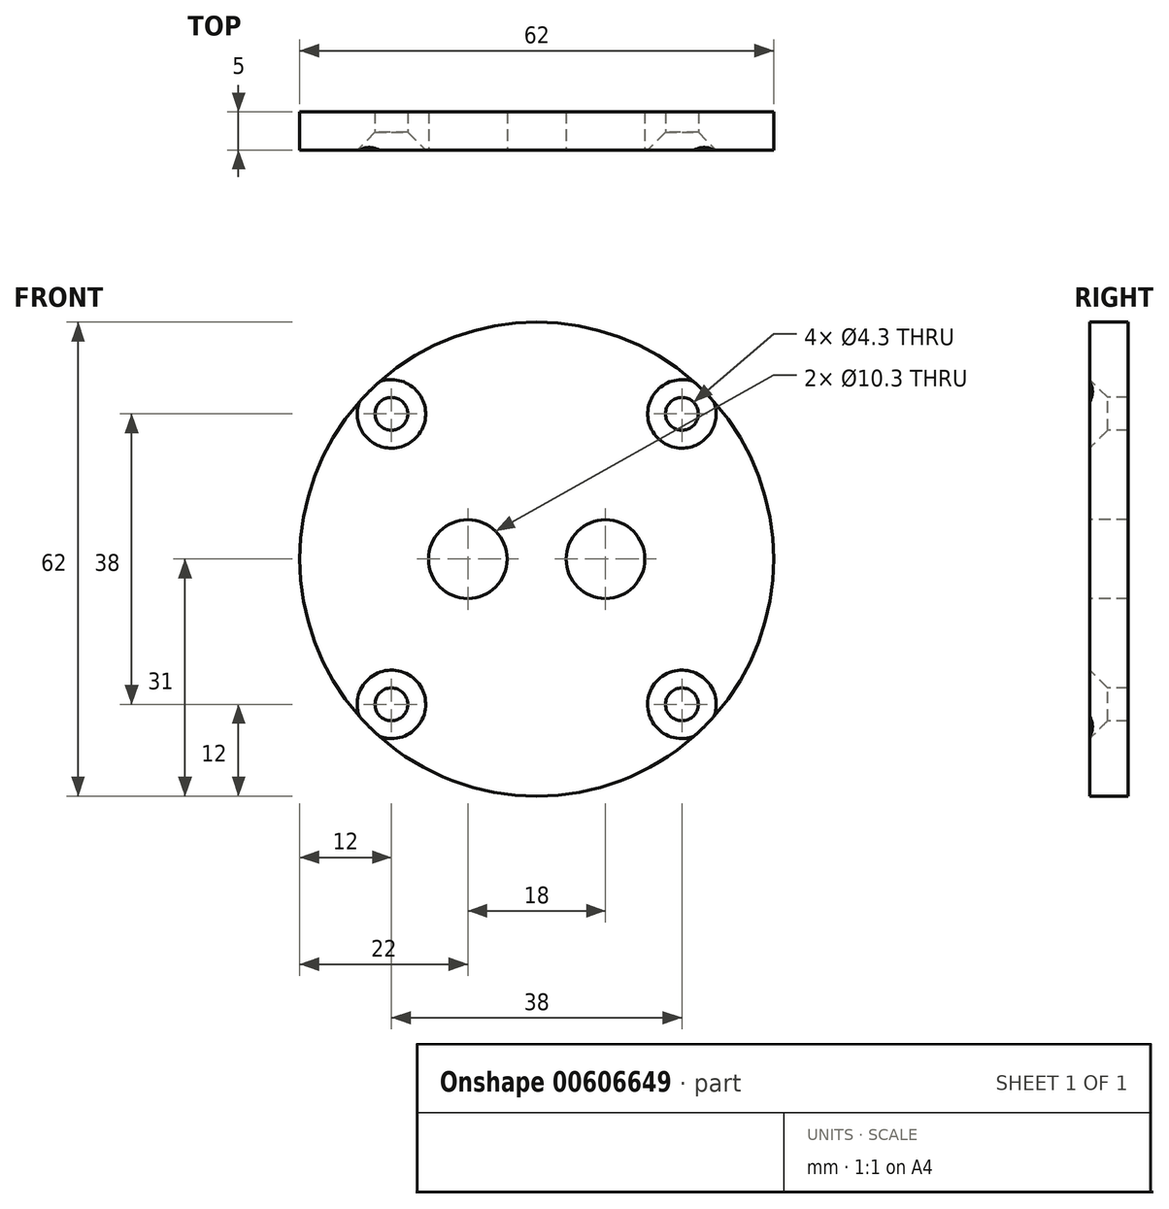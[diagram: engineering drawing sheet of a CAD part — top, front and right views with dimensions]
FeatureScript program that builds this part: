
annotation { "Feature Type Name" : "Feature", "Feature Type Description" : "" }
export const myFeature = defineFeature(function(context is Context, id is Id, definition is map)
    precondition{}
    {
        {
            var Q0;
            Q0=qCreatedBy(makeId("Front.planeOp"),FACE);
            var sketch = newSketch(context, id + "F0", { "sketchPlane" : qUnion([Q0])});
            skCircle(sketch, "E0", {"center": v(0, 0) * mm, "radius": 31 * mm});
            skPoint(sketch, "E1", {"position": v(-9, 0) * mm});
            skPoint(sketch, "E2", {"position": v(9, 0) * mm});
            skPoint(sketch, "E3", {"position": v(-19, 19) * mm});
            skPoint(sketch, "E4", {"position": v(19, 19) * mm});
            skPoint(sketch, "E5", {"position": v(-19, -19) * mm});
            skPoint(sketch, "E6", {"position": v(19, -19) * mm});
            skSolve(sketch);
        }
        {
            var Q0;
            Q0=qSketchRegion(id+"F0",true);
            var Q1;
            Q1=qConstructionFilter(qBodyType(qCreatedBy(id+"F0",EDGE),BodyType.WIRE),ConstructionObject.NO);
            extrude(context, id + "F1", {"entities" : qUnion([Q0]), "surfaceEntities" : qUnion([Q1]), "oppositeDirection" : true, "depth" : 5 * mm});
        }
        {
            var Q0;
            Q0=sQuery(id+"F0.wireOp",VERTEX,"E1");
            var Q1;
            Q1=sQuery(id+"F0.wireOp",VERTEX,"E2");
            var Q2;
            Q2=makeQuery(id+"F1.opExtrude","SWEPT_BODY",BODY,{"disambiguationData":[OSD([sQuery(id+"F0.wireOp",EDGE,"E0")])]});
            hole(context, id + "F2", {"style" : HoleStyle.SIMPLE, "endStyle" : HoleEndStyle.THROUGH, "standardTappedOrClearance" : lookupTablePath({ "standard" : "ISO", "engagement" : "75%", "pitch" : "1.75 mm", "size" : "M12", "type" : "Tapped" }), "standardBlindInLast" : lookupTablePath({ "standard" : "ISO", "engagement" : "75%", "pitch" : "1.75 mm", "size" : "M12", "type" : "Tapped" }), "holeDiameter" : 10.3 * mm, "showTappedDepth" : true, "isTappedThrough" : true, "tappedDepth" : 12 * mm, "tapClearance" : 3, "locations" : qUnion([Q0, Q1]), "scope" : qUnion([Q2]), "majorDiameter" : 12 * mm});
        }
        {
            var Q0;
            Q0=sQuery(id+"F0.wireOp",VERTEX,"E3");
            var Q1;
            Q1=sQuery(id+"F0.wireOp",VERTEX,"E4");
            var Q2;
            Q2=sQuery(id+"F0.wireOp",VERTEX,"E6");
            var Q3;
            Q3=sQuery(id+"F0.wireOp",VERTEX,"E5");
            var Q4;
            Q4=makeQuery(id+"F1.opExtrude","SWEPT_BODY",BODY,{"disambiguationData":[OSD([sQuery(id+"F0.wireOp",EDGE,"E0")])]});
            hole(context, id + "F3", {"style" : HoleStyle.C_SINK, "endStyle" : HoleEndStyle.THROUGH, "standardTappedOrClearance" : lookupTablePath({ "standard" : "ISO", "size" : "4.3", "type" : "Drilled" }), "standardBlindInLast" : lookupTablePath({ "standard" : "ISO", "size" : "4.3", "type" : "Drilled" }), "holeDiameter" : 4.3 * mm, "cSinkDiameter" : 8.96 * mm, "cSinkAngle" : 90 * degree, "isTappedThrough" : true, "tappedDepth" : 12 * mm, "tapClearance" : 3, "locations" : qUnion([Q0, Q1, Q2, Q3]), "scope" : qUnion([Q4])});
        }
    });
